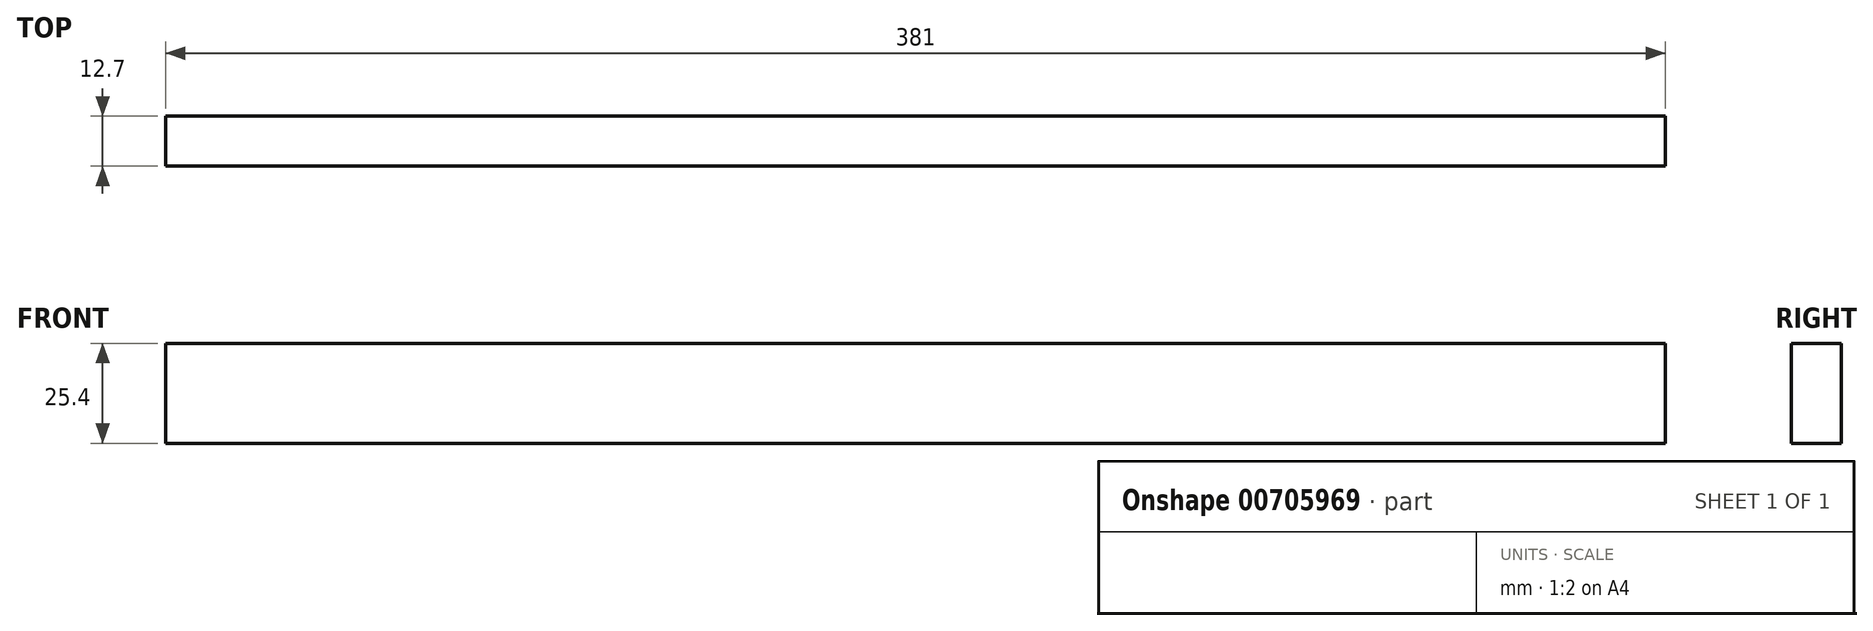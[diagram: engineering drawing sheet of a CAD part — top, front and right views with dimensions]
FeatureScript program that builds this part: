
annotation { "Feature Type Name" : "Feature", "Feature Type Description" : "" }
export const myFeature = defineFeature(function(context is Context, id is Id, definition is map)
    precondition{}
    {
        {
            var Q0;
            Q0=qCreatedBy(makeId("Top.planeOp"),FACE);
            var sketch = newSketch(context, id + "F0", { "sketchPlane" : qUnion([Q0])});
            skLineSegment(sketch, "E0.bottom", {"start": v(-70.28, 69) * mm, "end": v(310.72, 69) * mm});
            skLineSegment(sketch, "E0.top", {"start": v(-70.28, 56.3) * mm, "end": v(310.72, 56.3) * mm});
            skLineSegment(sketch, "E0.left", {"start": v(-70.28, 69) * mm, "end": v(-70.28, 56.3) * mm});
            skLineSegment(sketch, "E0.right", {"start": v(310.72, 69) * mm, "end": v(310.72, 56.3) * mm});
            skSolve(sketch);
        }
        {
            var Q0;
            Q0=makeQuery(id+"F0.imprint","IMPRINT",FACE,{"disambiguationData":[TD([[makeQuery(id+"F0.imprint","IMPRINT",EDGE,{"derivedFrom":sQuery(id+"F0.wireOp",EDGE,"E0.bottom")}),-1.0]])]});
            extrude(context, id + "F1", {"entities" : qUnion([Q0]), "depth" : 25.4 * mm, "offsetDistance" : 25.4 * mm});
        }
    });
